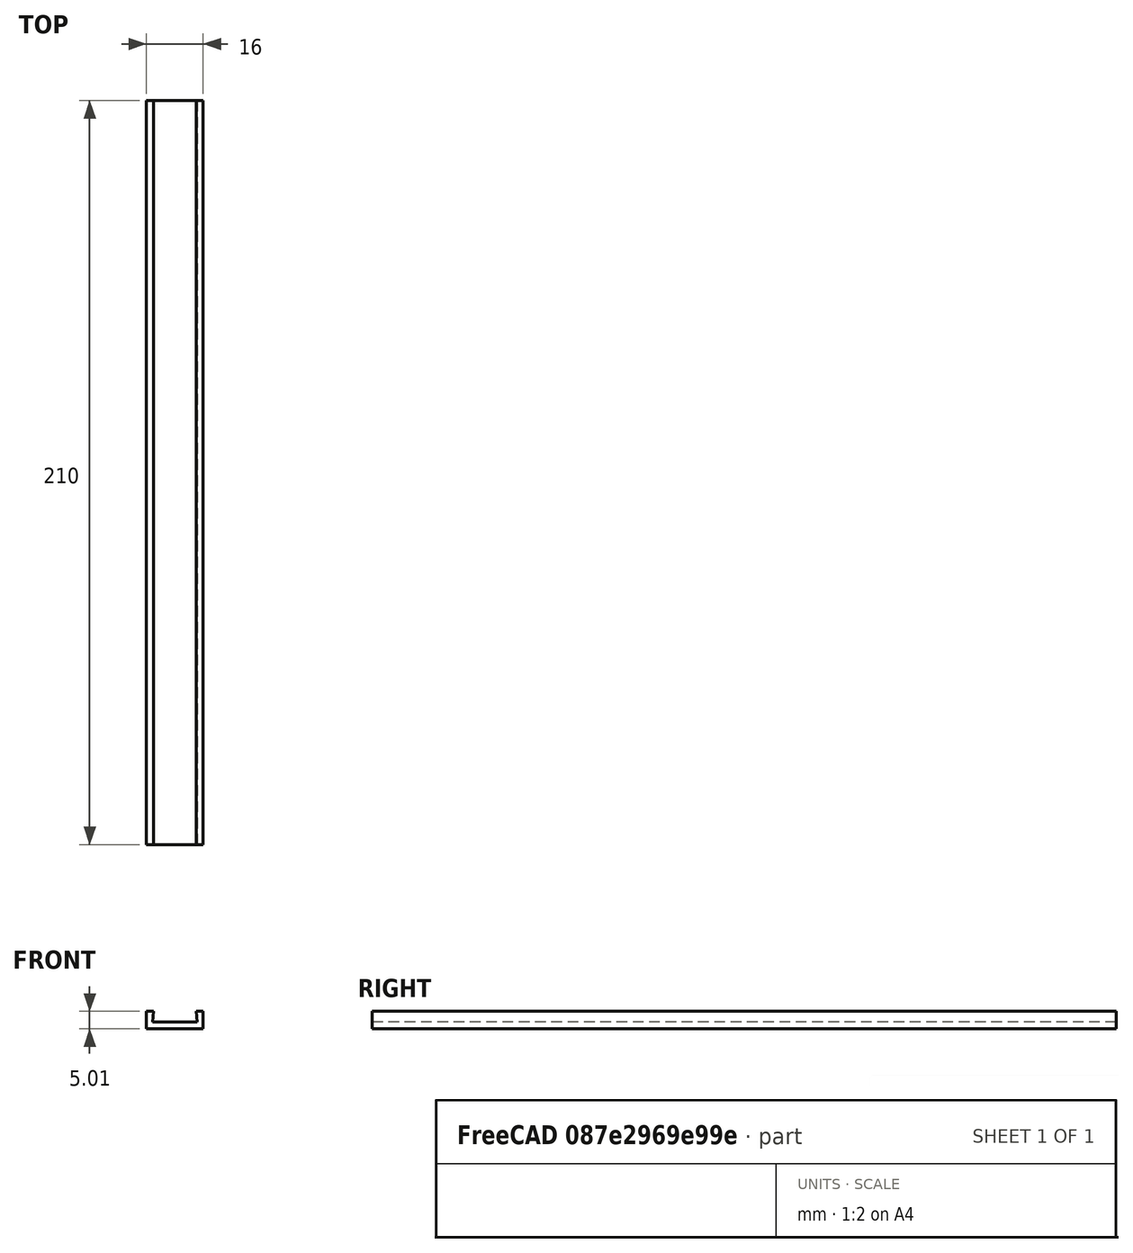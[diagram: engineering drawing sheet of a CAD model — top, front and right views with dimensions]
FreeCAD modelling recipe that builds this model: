
FCSTD DOCUMENT  (FreeCAD 0.21R33771 (Git))
Label: book spine
License: All rights reserved
LicenseURL: https://en.wikipedia.org/wiki/All_rights_reserved
objects: Sketcher::SketchObject×1, PartDesign::Pad×1, PartDesign::Body×1
note: 4 computed .brp shape members not serialized (recipe doc carries the construction recipe); baked Part::Feature solids carry a one-line shape summary decoded from their .brp

FEATURE [Sketcher::SketchObject] Sketch
  FullyConstrained = false
  MapMode = 5
  Placement = pos=(0,0,0) rot=(1,0,0;1.5708rad)
  Support = -> [XZ_Plane]
  sketch-geometry (8):
    g0: LineSegment StartX=-6 StartY=3 StartZ=0 EndX=-6.25 EndY=0 EndZ=0
    g1: LineSegment StartX=-6.25 StartY=0 StartZ=0 EndX=6.25 EndY=0 EndZ=0
    g2: LineSegment StartX=6.25 StartY=0 StartZ=0 EndX=6 EndY=3 EndZ=0
    g3: LineSegment StartX=6 StartY=3 StartZ=0 EndX=8.00001 EndY=3 EndZ=0
    g4: LineSegment StartX=8.00001 StartY=3 StartZ=0 EndX=8 EndY=-2 EndZ=0
    g5: LineSegment StartX=-8 StartY=-2 StartZ=0 EndX=-8 EndY=3.00583 EndZ=0
    g6: LineSegment StartX=-8 StartY=3.00583 StartZ=0 EndX=-6 EndY=3 EndZ=0
    g7: LineSegment StartX=-8 StartY=-2 StartZ=0 EndX=8 EndY=-2 EndZ=0
  constraints (20):
    c: PointOnObject(g0,g-1)
    c: Coincident(g0,g1)
    c: Coincident(g1,g2)
    c: Coincident(g2,g3)
    c: Coincident(g3,g4)
    c: Coincident(g5,g6)
    c: Coincident(g6,g0)
    c: DistanceX(g1,g1) = 12.5
    c: Symmetric(g0,g1,g-1)
    c: DistanceY(g4,g1) = 2
    c: DistanceX(g5,g4) = 16
    c: Symmetric(g5,g4,g-2)
    c: Equal(g6,g3)
    c: DistanceX(g6,g6) = 2
    c: Horizontal(g3)
    c: Coincident(g7,g5)
    c: Coincident(g7,g4)
    c: DistanceX(g0,g2) = 12
    c: Symmetric(g0,g2,g-2)
    c: DistanceY(g1,g2) = 3
FEATURE [PartDesign::Pad] Pad
  Direction = (0,-1,-2e-16)
  Length = 210
  Length2 = 10
  Placement = pos=(0,0,0) rot=(1,0,0;1.5708rad)
  Profile = -> Sketch
  ReferenceAxis = -> Sketch [N_Axis]
  Type = 0
FEATURE [PartDesign::Body] Body
  Group = -> [Sketch,Pad]
  Origin = -> Origin
  Tip = -> Pad
